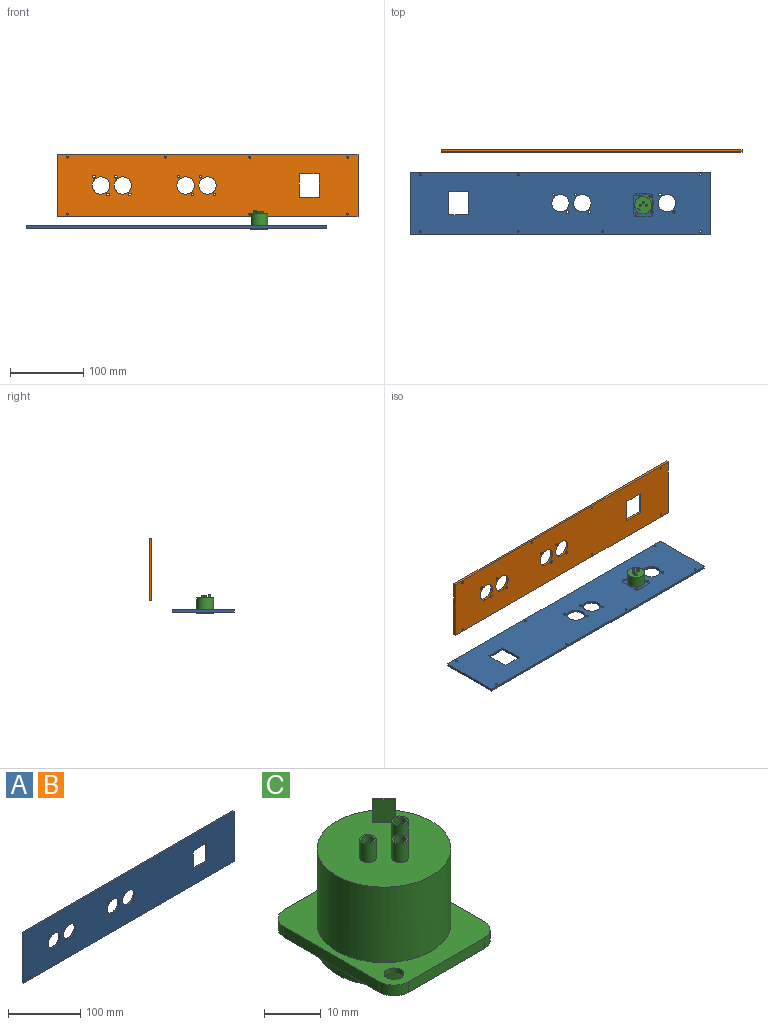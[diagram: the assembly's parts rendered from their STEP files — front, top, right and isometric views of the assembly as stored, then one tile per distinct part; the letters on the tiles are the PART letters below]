
ASSEMBLY  parts=3 mates=1
PART A: 29 faces, bbox 411.8x3x85 mm
  f0: plane 85x3mm, normal (-1,0,0), area 255mm2, adj f1,f26,f27,f28
  f1: plane 411.8x3mm, normal (0,0,-1), area 1235.4mm2, adj f0,f2,f27,f28
  f2: plane 85x3mm, normal (1,0,0), area 255mm2, adj f1,f26,f27,f28
  f3: plane 27x3mm, normal (0,0,-1), area 81mm2, adj f4,f6,f27,f28
  f4: plane 32x3mm, normal (-1,0,0), area 96mm2, adj f3,f5,f27,f28
  f5: plane 27x3mm, normal (0,0,1), area 81mm2, adj f4,f6,f27,f28
  f6: plane 32x3mm, normal (1,0,0), area 96mm2, adj f3,f5,f27,f28
  f7: cylinder r=1.35mm len=3mm, axis (0,1,0), area 25.4mm2, adj f27,f28
  f8: cylinder r=1.35mm len=3mm, axis (0,1,0), area 25.4mm2, adj f27,f28
  f9: cylinder r=1.35mm len=3mm, axis (0,1,0), area 25.4mm2, adj f27,f28
  f10: cylinder r=1.35mm len=3mm, axis (0,1,0), area 25.4mm2, adj f27,f28
  f11: cylinder r=1.35mm len=3mm, axis (0,1,0), area 25.4mm2, adj f27,f28
  f12: cylinder r=1.35mm len=3mm, axis (0,1,0), area 25.4mm2, adj f27,f28
  f13: cylinder r=1.35mm len=3mm, axis (0,1,0), area 25.4mm2, adj f27,f28
  f14: cylinder r=11.85mm len=23.7mm, axis (0,1,0), area 223.4mm2, adj f27,f28
  f15: cylinder r=1.8mm len=3.6mm, axis (0,1,0), area 33.9mm2, adj f27,f28
  f16: cylinder r=1.8mm len=3.6mm, axis (0,1,0), area 33.9mm2, adj f27,f28
  f17: cylinder r=11.85mm len=23.7mm, axis (0,1,0), area 223.4mm2, adj f27,f28
  f18: cylinder r=1.8mm len=3.6mm, axis (0,1,0), area 33.9mm2, adj f27,f28
  f19: cylinder r=1.8mm len=3.6mm, axis (0,1,0), area 33.9mm2, adj f27,f28
  f20: cylinder r=11.85mm len=23.7mm, axis (0,1,0), area 223.4mm2, adj f27,f28
  f21: cylinder r=1.8mm len=3.6mm, axis (0,1,0), area 33.9mm2, adj f27,f28
  f22: cylinder r=1.8mm len=3.6mm, axis (0,1,0), area 33.9mm2, adj f27,f28
  f23: cylinder r=11.85mm len=23.7mm, axis (0,1,0), area 223.4mm2, adj f27,f28
  f24: cylinder r=1.8mm len=3.6mm, axis (0,1,0), area 33.9mm2, adj f27,f28
  f25: cylinder r=1.8mm len=3.6mm, axis (0,1,0), area 33.9mm2, adj f27,f28
  f26: plane 411.8x3mm, normal (0,0,1), area 1235.4mm2, adj f0,f2,f27,f28
  f27: plane 411.8x85mm, normal (0,-1,0), area 32252.9mm2, adj f0,f1,f2,f3,f4,f5,f6,f7
  f28: plane 411.8x85mm, normal (0,1,0), area 32252.9mm2, adj f0,f1,f2,f3,f4,f5,f6,f7
PART B: same geometry as A
PART C: 44 faces, bbox 26x31x26.3 mm
  f0: plane 31x26mm, normal (0,0,-1), area 301.5mm2, adj f1,f2,f3,f4,f5,f6,f7,f8
  f1: plane 24x2.3mm, normal (-1,0,0), area 55.2mm2, adj f0,f2,f8,f9
  f2: cylinder r=3.5mm len=3.5mm, axis (0,0,1), area 12.6mm2, adj f0,f1,f3,f9
  f3: plane 19x2.3mm, normal (0,1,0), area 43.7mm2, adj f0,f2,f4,f9
  f4: cylinder r=3.5mm len=3.5mm, axis (0,0,1), area 12.6mm2, adj f0,f3,f5,f9
  f5: plane 24x2.3mm, normal (1,0,0), area 55.2mm2, adj f0,f4,f6,f9
  f6: cylinder r=3.5mm len=3.5mm, axis (0,0,1), area 12.6mm2, adj f0,f5,f7,f9
  f7: plane 19x2.3mm, normal (0,-1,0), area 43.7mm2, adj f0,f6,f8,f9
  f8: cylinder r=3.5mm len=3.5mm, axis (0,0,1), area 12.6mm2, adj f0,f1,f7,f9
  f9: plane 31x26mm, normal (0,0,1), area 338.8mm2, adj f1,f2,f3,f4,f5,f6,f7,f8
  f10: cylinder r=1.75mm len=3.5mm, axis (0,0,1), area 11.5mm2, adj f9,f11
  f11: cone r=2.37mm half-angle=45deg, axis (0,0,-1), area 26.4mm2, adj f0,f10
  f12: cylinder r=1.75mm len=3.5mm, axis (0,0,1), area 11.5mm2, adj f9,f13
  f13: cone r=2.37mm half-angle=45deg, axis (0,0,-1), area 26.4mm2, adj f0,f12
  f14: cylinder r=11.8mm len=23.6mm, axis (0,0,-1), area 200.2mm2, adj f0,f16
  f15: cylinder r=11.8mm len=23.6mm, axis (0,0,-1), area 1208.5mm2, adj f9,f26
  f16: plane 23.6x23.6mm, normal (0,0,-1), area 225.3mm2, adj f14,f24,f25
  f17: plane 2.38x2.38mm, normal (0,0,-1), area 4.4mm2, adj f20
  f18: plane 2.38x2.38mm, normal (0,0,-1), area 4.4mm2, adj f22
  f19: plane 2.38x2.38mm, normal (0,0,-1), area 4.4mm2, adj f23
  f20: cylinder r=1.19mm len=13.7mm, axis (0,0,-1), area 102.4mm2, adj f17,f21
  f21: plane 16.4x16.4mm, normal (0,0,-1), area 198.8mm2, adj f20,f22,f23,f24,f25
  f22: cylinder r=1.19mm len=13.7mm, axis (0,0,-1), area 102.4mm2, adj f18,f21
  f23: cylinder r=1.19mm len=13.7mm, axis (0,0,-1), area 102.4mm2, adj f19,f21
  f24: cylinder r=8.2mm len=16.4mm, axis (0,0,-1), area 685.3mm2, adj f16,f21,f25
  f25: cylinder r=0.75mm len=13.7mm, axis (0,0,-1), area 33.2mm2, adj f16,f21,f24
  f26: plane 23.6x23.6mm, normal (0,0,1), area 415.6mm2, adj f15,f30,f31,f32,f33,f39,f41,f43
  f27: plane 2.2x2.2mm, normal (0,0,1), area 3.8mm2, adj f35
  f28: plane 2.2x2.2mm, normal (0,0,1), area 3.8mm2, adj f40
  f29: plane 2.2x2.2mm, normal (0,0,1), area 3.8mm2, adj f42
  f30: plane 5x0.35mm, normal (-0.71,0.71,0), area 2.5mm2, adj f26,f31,f33,f34
  f31: plane 5x2.83mm, normal (0.71,0.71,0), area 20mm2, adj f26,f30,f32,f34
  f32: plane 5x0.35mm, normal (0.71,-0.71,0), area 2.5mm2, adj f26,f31,f33,f34
  f33: plane 5x2.83mm, normal (-0.71,-0.71,0), area 20mm2, adj f26,f30,f32,f34
  f34: plane 3.18x3.18mm, normal (0,0,1), area 2mm2, adj f30,f31,f32,f33
  f35: cylinder r=1.1mm len=4mm, axis (0,0,1), area 27.6mm2, adj f27,f36
  f36: plane 2.9x2.9mm, normal (0,0,1), area 2.8mm2, adj f35,f39
  f37: plane 2.9x2.9mm, normal (0,0,1), area 2.8mm2, adj f40,f41
  f38: plane 2.9x2.9mm, normal (0,0,1), area 2.8mm2, adj f42,f43
  f39: cylinder r=1.45mm len=4mm, axis (0,0,1), area 36.4mm2, adj f26,f36
  f40: cylinder r=1.1mm len=4mm, axis (0,0,1), area 27.6mm2, adj f28,f37
  f41: cylinder r=1.45mm len=4mm, axis (0,0,1), area 36.4mm2, adj f26,f37
  f42: cylinder r=1.1mm len=4mm, axis (0,0,1), area 27.6mm2, adj f29,f38
  f43: cylinder r=1.45mm len=4mm, axis (0,0,1), area 36.4mm2, adj f26,f38
PLACE A rot(axis=(0,0.71,-0.71),180deg) t=(-42.59,-72.99,-58.18)mm
PLACE B at identity
PLACE C rot(axis=(0,0,-1),180deg) t=(70.72,-75.74,-57.48)mm
MATE planar A.f27 <-> C.f8  axis (0,0,1) through (-43.02,-72.99,-55.18)mm
